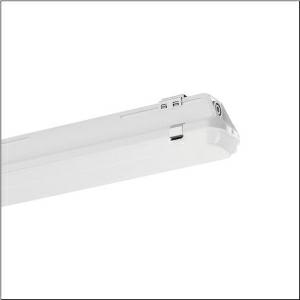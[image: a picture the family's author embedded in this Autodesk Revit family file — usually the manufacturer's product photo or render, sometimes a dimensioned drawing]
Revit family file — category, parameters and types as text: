
# Revit family: monsun_11_51fp11mp4b0u
name_source: partatom
category: Lighting Fixtures
units: mm (PartAtom-declared; Revit-internal decimal feet)

## family parameters
Cut with Voids When Loaded = No
Host = Face
Light Source = No
Part Type = Normal
Room Calculation Point = No
Round Connector Dimension = Use Diameter
Shared = No

## types (1)
- --- (1 x LED, 11900 lm, 62.4 W, 4000K)
    Apparent Load = 62 VA
    CIE Flux Codes = 71 88 97 97 100
    Color Rendering = 80
    Color Temperature = 4000K
    Default Elevation = 1800 mm
    Description = Monsun 11, damp-proof luminaire, chain hanger, primary optical cover: enclosure, of PMMA, light emission: direct distribution, primary light characteristic: symmetric, installation type: suspended mounting, surface-mounted, horizontal mounting, vertical mounting, LED, rated luminous flux: 11.900lm, luminous efficacy: 191lm/W, light colour: 840, colour temperature: 4000K, control gear: ON/OFF Multilumen, with terminal, 3-pole, max. 2.5mm², mains connection: 220..240V, AC, 50/60Hz, rated input power: 62W, luminaire housing, of glass-fibre reinforced polyester, uncoated, bright grey, incl. chain hanger, length: 1.590mm, width: 90mm, height: 88mm, clip for enclosure, of stainless steel (V2A), ceiling mounting element, of stainless steel (V2A), chain hanger, of stainless steel (V2A), protection rating (complete): IP66, insulation class (complete): insulation class I (protective earthing), certification: CE, ENEC, VDE, UKCA, protection symbol: D, impact resistance: IK04, permissible operating ambient temperature: -35..+35°C, standard: EN 50419, EN 60598-2-1, contact your sales advisor before using the luminaires in applications with unclear chemical exposure, large temperature fluctuations or condensation-forming humidity, LABS conformity tested according to VDMA 24364:2018-05, no direct snow, no direct sun, no direct rain, for indoor or canopied outdoor use, corresponds to IFS (International Featured Standards) requirements for safety and quality in the food industry, packaging unit: 1 piece
    Height = 89 mm
    Lamp = 1 x LED
    Lamp Light Flux = 11900 lm
    Lamp Power = 62.4 W
    Lamp count = 1
    Length = 1590 mm
    Luminous efficacy = 191 lm/W
    Manufacturer = Siteco
    ModVariant = No
    Model = 51FP11MP4B0U
    Mounting Place = Ceiling
    Mounting Type = Surface mounted
    Number of Poles = 1
    OnlyDefault = Yes
    Power Factor = 1
    Product Name = Monsun 11
    Product group = damp-proof luminaire
    ProductGroupID = 300
    Protection Class = Protection class I
    Protection Degree = IP 66
    RLX_Detail_Level = 1
    RLX_Emergency_Light_Flux = 0 lm
    RLX_Emergency_Type = 0
    RLX_Emergency_Type_DB = No
    RlxData = <blob elided: 89801 chars, md5=4c2863e8>
    Socket = socket
    Standby Power = 0 W
    System Light Flux = 11900 lm
    System Power = 62 W
    Type Comments = factory setting: luminous flux: 100 % | (A | C | E) | 147 mA
    Type Image = l_1349237.jpg
    URL = http://relux.com
    VarID = @adj_000033
    Voltage = 0 V
    Weight = 0.00 kg
    Width = 90 mm

## geometry (parser evidence)
native form markers: Blend x4, Sweep x10
no freeform markers — native parametric forms only
